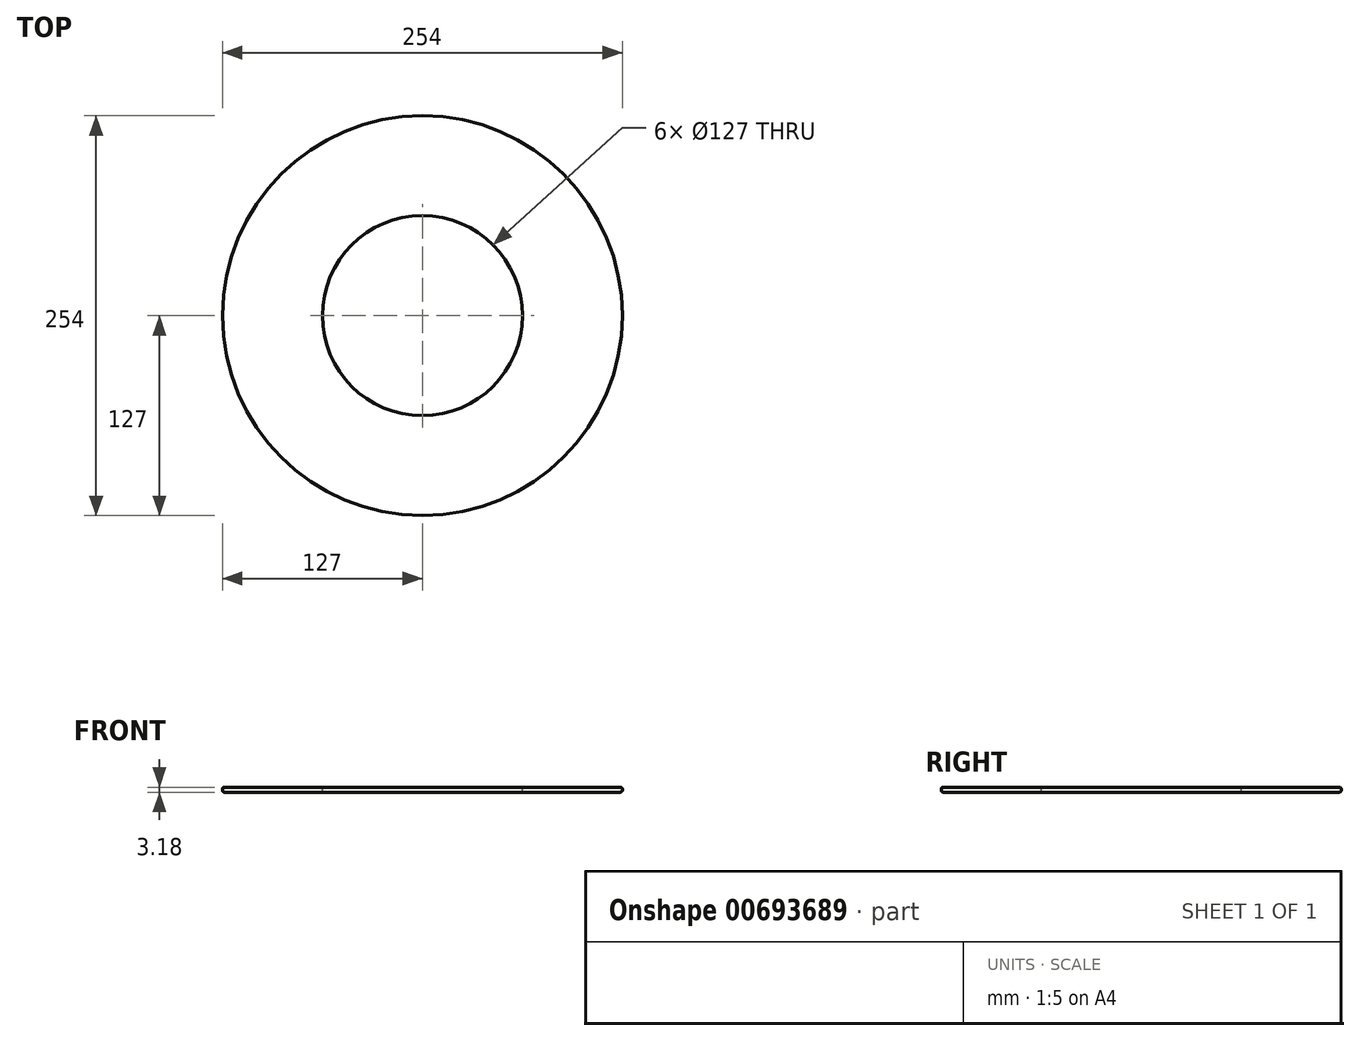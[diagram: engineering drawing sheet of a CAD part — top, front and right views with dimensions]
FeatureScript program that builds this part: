
annotation { "Feature Type Name" : "Feature", "Feature Type Description" : "" }
export const myFeature = defineFeature(function(context is Context, id is Id, definition is map)
    precondition{}
    {
        {
            var Q0;
            Q0=qCreatedBy(makeId("Front.planeOp"),FACE);
            var sketch = newSketch(context, id + "F0", { "sketchPlane" : qUnion([Q0])});
            skLineSegment(sketch, "E0.bottom", {"start": v(31.75, 1.59) * mm, "end": v(-31.75, 1.59) * mm});
            skLineSegment(sketch, "E0.top", {"start": v(31.75, -1.59) * mm, "end": v(-31.75, -1.59) * mm});
            skLineSegment(sketch, "E0.left", {"start": v(31.75, 1.59) * mm, "end": v(31.75, -1.59) * mm});
            skLineSegment(sketch, "E0.right", {"start": v(-31.75, 1.59) * mm, "end": v(-31.75, -1.59) * mm});
            skPoint(sketch, "E0.middle", {"position": v(0, 0) * mm});
            skLineSegment(sketch, "E1", {"start": v(95.25, 45.24) * mm, "end": v(95.25, -57.66) * mm, "construction": true});
            skSolve(sketch);
        }
        {
            var Q0;
            Q0 = qSketchRegion(id + "F0", true);
            var Q1;
            Q1=sQuery(id+"F0.wireOp",EDGE,"E1");
            revolve(context, id + "F1", {"entities" : qUnion([Q0]), "axis" : qUnion([Q1]), "revolveType" : RevolveType.FULL});
        }
        {
            var Q0;
            Q0=makeQuery(id+"F1.opRevolve","SWEPT_EDGE",EDGE,{"disambiguationData":[OSD([sQuery(id+"F0.wireOp",EDGE,"E0.top"),sQuery(id+"F0.wireOp",EDGE,"E0.right")])]});
            var Q1;
            Q1=makeQuery(id+"F1.opRevolve","SWEPT_EDGE",EDGE,{"disambiguationData":[OSD([sQuery(id+"F0.wireOp",EDGE,"E0.bottom"),sQuery(id+"F0.wireOp",EDGE,"E0.right")])]});
            fillet(context, id + "F2", {"entities" : qUnion([Q0, Q1]), "radius" : 1.27 * mm, "tangentPropagation" : true, "allowEdgeOverflow" : false});
        }
    });
